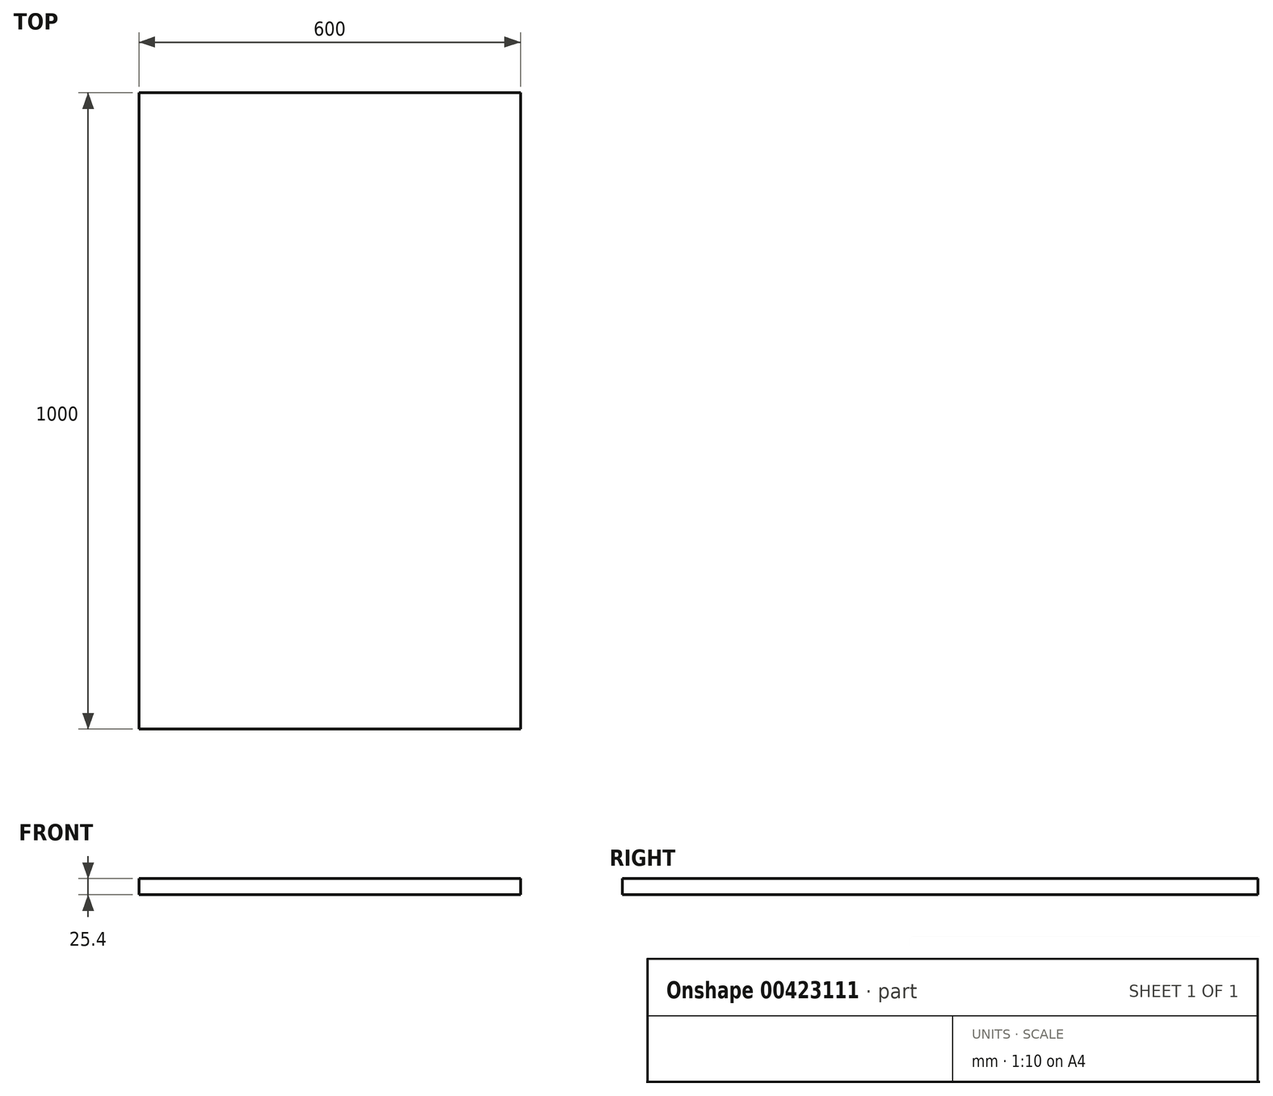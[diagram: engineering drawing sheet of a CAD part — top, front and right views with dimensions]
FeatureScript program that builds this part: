
annotation { "Feature Type Name" : "Feature", "Feature Type Description" : "" }
export const myFeature = defineFeature(function(context is Context, id is Id, definition is map)
    precondition{}
    {
        {
            var Q0;
            Q0=qCreatedBy(makeId("Top.planeOp"),FACE);
            var sketch = newSketch(context, id + "F0", { "sketchPlane" : qUnion([Q0])});
            skLineSegment(sketch, "E0.bottom", {"start": v(0, 0) * mm, "end": v(0, 0) * mm});
            skLineSegment(sketch, "E0.top", {"start": v(0, 0) * mm, "end": v(0, 0) * mm});
            skLineSegment(sketch, "E0.left", {"start": v(0, 0) * mm, "end": v(0, 0) * mm});
            skLineSegment(sketch, "E0.right", {"start": v(0, 0) * mm, "end": v(0, 0) * mm});
            skLineSegment(sketch, "E1.bottom", {"start": v(600, 1000) * mm, "end": v(0, 1000) * mm});
            skLineSegment(sketch, "E1.top", {"start": v(600, 0) * mm, "end": v(0, 0) * mm});
            skLineSegment(sketch, "E1.left", {"start": v(600, 1000) * mm, "end": v(600, 0) * mm});
            skLineSegment(sketch, "E1.right", {"start": v(0, 1000) * mm, "end": v(0, 0) * mm});
            skSolve(sketch);
        }
        {
            var Q0;
            Q0=makeQuery(id+"F0.imprint","IMPRINT",FACE,{"disambiguationData":[TD([[makeQuery(id+"F0.imprint","IMPRINT",EDGE,{"derivedFrom":sQuery(id+"F0.wireOp",EDGE,"E1.bottom")}),1.0]])]});
            extrude(context, id + "F1", {"entities" : qUnion([Q0]), "depth" : 25.4 * mm});
        }
    });
